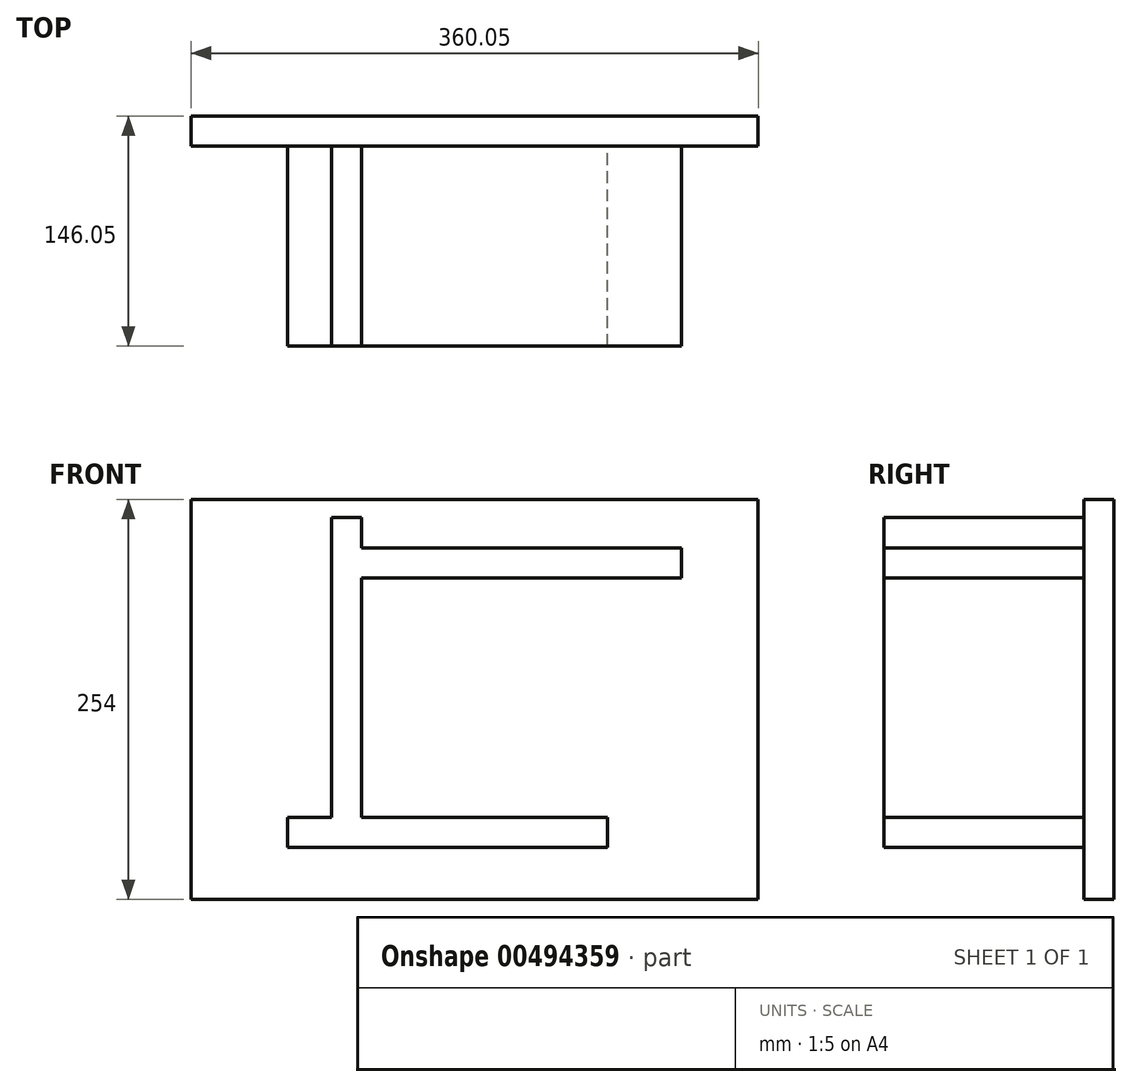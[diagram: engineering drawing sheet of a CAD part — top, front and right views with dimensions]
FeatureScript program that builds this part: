
annotation { "Feature Type Name" : "Feature", "Feature Type Description" : "" }
export const myFeature = defineFeature(function(context is Context, id is Id, definition is map)
    precondition{}
    {
        {
            var Q0;
            Q0=qCreatedBy(makeId("Front.planeOp"),FACE);
            var sketch = newSketch(context, id + "F0", { "sketchPlane" : qUnion([Q0])});
            skLineSegment(sketch, "E0.bottom", {"start": v(-99, 81.65) * mm, "end": v(-79.94, 81.65) * mm});
            skLineSegment(sketch, "E0.top", {"start": v(-99, -108.85) * mm, "end": v(-79.94, -108.85) * mm});
            skLineSegment(sketch, "E0.left", {"start": v(-99, 81.65) * mm, "end": v(-99, -108.85) * mm});
            skLineSegment(sketch, "E0.right", {"start": v(-79.94, 81.65) * mm, "end": v(-79.94, -108.85) * mm});
            skLineSegment(sketch, "E1.bottom", {"start": v(-79.94, 62.43) * mm, "end": v(123.26, 62.43) * mm});
            skLineSegment(sketch, "E1.top", {"start": v(-79.94, 43.38) * mm, "end": v(123.26, 43.38) * mm});
            skLineSegment(sketch, "E1.left", {"start": v(-79.94, 62.43) * mm, "end": v(-79.94, 43.38) * mm});
            skLineSegment(sketch, "E1.right", {"start": v(123.26, 62.43) * mm, "end": v(123.26, 43.38) * mm});
            skLineSegment(sketch, "E2.bottom", {"start": v(76.24, 43.38) * mm, "end": v(95.29, 43.38) * mm});
            skLineSegment(sketch, "E2.top", {"start": v(76.24, -147.12) * mm, "end": v(95.29, -147.12) * mm});
            skLineSegment(sketch, "E2.left", {"start": v(76.24, 43.38) * mm, "end": v(76.24, -147.12) * mm});
            skLineSegment(sketch, "E2.right", {"start": v(95.29, 43.38) * mm, "end": v(95.29, -147.12) * mm});
            skLineSegment(sketch, "E3.bottom", {"start": v(-126.96, -108.85) * mm, "end": v(76.24, -108.85) * mm});
            skLineSegment(sketch, "E3.top", {"start": v(-126.96, -127.9) * mm, "end": v(76.24, -127.9) * mm});
            skLineSegment(sketch, "E3.left", {"start": v(-126.96, -108.85) * mm, "end": v(-126.96, -127.9) * mm});
            skLineSegment(sketch, "E3.right", {"start": v(76.24, -108.85) * mm, "end": v(76.24, -127.9) * mm});
            skSolve(sketch);
        }
        {
            var Q0;
            {var subQ4=sQuery(id+"F0.wireOp",EDGE,"E0.bottom");Q0=makeQuery(id+"F0.imprint","IMPRINT",FACE,{"disambiguationData":[TD([[makeQuery(id+"F0.imprint","IMPRINT",EDGE,{"derivedFrom":subQ4}),-1.0]])]});}
            var Q1;
            Q1=makeQuery(id+"F0.imprint","IMPRINT",FACE,{"disambiguationData":[TD([[makeQuery(id+"F0.imprint","IMPRINT",EDGE,{"derivedFrom":sQuery(id+"F0.wireOp",EDGE,"E1.bottom")}),-1.0]])]});
            var Q2;
            {var subQ3=sQuery(id+"F0.wireOp",EDGE,"E2.bottom");Q2=makeQuery(id+"F0.imprint","IMPRINT",FACE,{"disambiguationData":[TD([[makeQuery(id+"F0.imprint","IMPRINT",EDGE,{"derivedFrom":subQ3}),-1.0]])]});}
            var Q3;
            Q3=makeQuery(id+"F0.imprint","IMPRINT",FACE,{"disambiguationData":[TD([[makeQuery(id+"F0.imprint","IMPRINT",EDGE,{"derivedFrom":sQuery(id+"F0.wireOp",EDGE,"E3.top")}),1.0]])]});
            extrude(context, id + "F1", {"entities" : qUnion([Q0, Q1, Q2, Q3]), "depth" : 127 * mm});
        }
        {
            var Q0;
            Q0=makeQuery(id+"F1.opExtrude","CAP_FACE",FACE,{"disambiguationData":[OSD([sQuery(id+"F0.wireOp",EDGE,"E0.bottom"),sQuery(id+"F0.wireOp",EDGE,"E0.left"),sQuery(id+"F0.wireOp",EDGE,"E0.right"),sQuery(id+"F0.wireOp",EDGE,"E1.bottom"),sQuery(id+"F0.wireOp",EDGE,"E1.top"),sQuery(id+"F0.wireOp",EDGE,"E1.right"),sQuery(id+"F0.wireOp",EDGE,"E2.top"),sQuery(id+"F0.wireOp",EDGE,"E2.left"),sQuery(id+"F0.wireOp",EDGE,"E2.right"),sQuery(id+"F0.wireOp",EDGE,"E3.bottom"),sQuery(id+"F0.wireOp",EDGE,"E3.top"),sQuery(id+"F0.wireOp",EDGE,"E3.left")])],"isStart":true});
            var sketch = newSketch(context, id + "F2", { "sketchPlane" : qUnion([Q0])});
            skLineSegment(sketch, "E4.bottom", {"start": v(-171.96, 93.1) * mm, "end": v(188.1, 93.1) * mm});
            skLineSegment(sketch, "E4.top", {"start": v(-171.96, -160.9) * mm, "end": v(188.1, -160.9) * mm});
            skLineSegment(sketch, "E4.left", {"start": v(-171.96, 93.1) * mm, "end": v(-171.96, -160.9) * mm});
            skLineSegment(sketch, "E4.right", {"start": v(188.1, 93.1) * mm, "end": v(188.1, -160.9) * mm});
            skSolve(sketch);
        }
        {
            var Q0;
            Q0=makeQuery(id+"F2.imprint","IMPRINT",FACE,{"disambiguationData":[TD([[makeQuery(id+"F2.imprint","IMPRINT",EDGE,{"derivedFrom":sQuery(id+"F2.wireOp",EDGE,"E4.bottom")}),-1.0]])]});
            var Q1;
            {var subQ0=sQuery(id+"F0.wireOp",EDGE,"E3.bottom");var subQ1=sQuery(id+"F0.wireOp",EDGE,"E0.right");var subQ2=makeQuery(id+"F0.imprint","INTERSECT",VERTEX,{"derivedFrom":[subQ1,subQ0]});Q1=makeQuery(id+"F2.imprint","IMPRINT",FACE,{"disambiguationData":[TD([[makeQuery(id+"F2.imprint","IMPRINT",EDGE,{"derivedFrom":makeQuery(id+"F1.opExtrude","CAP_EDGE",EDGE,{"disambiguationData":[OSD([subQ1]),TDD([makeQuery(id+"F0.imprint","IMPRINT",EDGE,{"disambiguationData":[TD([[subQ2,1.0]])],"derivedFrom":subQ1})])],"isStart":true})}),-1.0]])]});}
            var Q2;
            {var subQ14=sQuery(id+"F0.wireOp",EDGE,"E0.bottom");Q2=makeQuery(id+"F2.imprint","IMPRINT",FACE,{"disambiguationData":[TD([[makeQuery(id+"F2.imprint","IMPRINT",EDGE,{"derivedFrom":makeQuery(id+"F1.opExtrude","CAP_EDGE",EDGE,{"disambiguationData":[OSD([subQ14])],"isStart":true})}),1.0]])]});}
            extrude(context, id + "F3", {"entities" : qUnion([Q0, Q1, Q2]), "operationType" : NewBodyOperationType.ADD, "depth" : 19.05 * mm});
        }
    });
